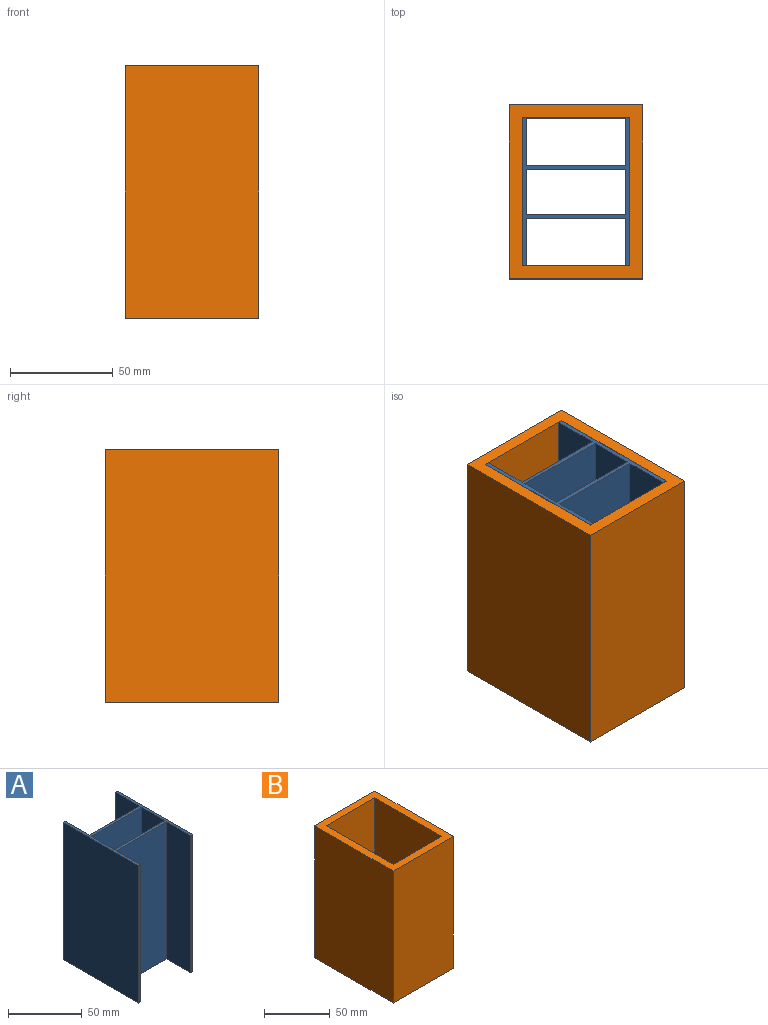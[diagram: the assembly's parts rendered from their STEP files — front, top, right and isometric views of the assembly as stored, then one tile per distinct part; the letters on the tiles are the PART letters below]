
ASSEMBLY  parts=2 mates=1
PART A: 18 faces, bbox 52.2x72x113.6 mm
  f0: plane 113.6x48.2mm, normal (0,1,0), area 5475.5mm2, adj f1,f15,f16,f17
  f1: plane 113.6x22mm, normal (1,0,0), area 2499.2mm2, adj f0,f2,f16,f17
  f2: plane 113.6x48.2mm, normal (0,-1,0), area 5475.5mm2, adj f1,f15,f16,f17
  f3: plane 113.6x72mm, normal (-1,0,0), area 8179.2mm2, adj f4,f14,f16,f17
  f4: plane 113.6x2mm, normal (0,-1,0), area 227.2mm2, adj f3,f5,f16,f17
  f5: plane 113.6x23mm, normal (1,0,0), area 2612.8mm2, adj f4,f6,f16,f17
  f6: plane 113.6x48.2mm, normal (0,-1,0), area 5475.5mm2, adj f5,f7,f16,f17
  f7: plane 113.6x23mm, normal (-1,0,0), area 2612.8mm2, adj f6,f8,f16,f17
  f8: plane 113.6x2mm, normal (0,-1,0), area 227.2mm2, adj f7,f9,f16,f17
  f9: plane 113.6x72mm, normal (1,0,0), area 8179.2mm2, adj f8,f10,f16,f17
  f10: plane 113.6x2mm, normal (0,1,0), area 227.2mm2, adj f9,f11,f16,f17
  f11: plane 113.6x23mm, normal (-1,0,0), area 2612.8mm2, adj f10,f12,f16,f17
  f12: plane 113.6x48.2mm, normal (0,1,0), area 5475.5mm2, adj f11,f13,f16,f17
  f13: plane 113.6x23mm, normal (1,0,0), area 2612.8mm2, adj f12,f14,f16,f17
  f14: plane 113.6x2mm, normal (0,1,0), area 227.2mm2, adj f3,f13,f16,f17
  f15: plane 113.6x22mm, normal (-1,0,0), area 2499.2mm2, adj f0,f2,f16,f17
  f16: plane 72x52.2mm, normal (0,0,1), area 480.8mm2, adj f0,f1,f2,f3,f4,f5,f6,f7
  f17: plane 72x52.2mm, normal (0,0,-1), area 480.8mm2, adj f0,f1,f2,f3,f4,f5,f6,f7
PART B: 10 faces, bbox 64.9x84.6x123 mm
  f0: plane 123x52.46mm, normal (0,1,0), area 6452.6mm2, adj f1,f7,f8,f9
  f1: plane 123x72.18mm, normal (1,0,0), area 8878.1mm2, adj f0,f2,f8,f9
  f2: plane 123x52.46mm, normal (0,-1,0), area 6452.6mm2, adj f1,f7,f8,f9
  f3: plane 123x84.6mm, normal (-1,0,0), area 10405.8mm2, adj f4,f6,f8,f9
  f4: plane 123x64.88mm, normal (0,-1,0), area 7980.2mm2, adj f3,f5,f8,f9
  f5: plane 123x84.6mm, normal (1,0,0), area 10405.8mm2, adj f4,f6,f8,f9
  f6: plane 123x64.88mm, normal (0,1,0), area 7980.2mm2, adj f3,f5,f8,f9
  f7: plane 123x72.18mm, normal (-1,0,0), area 8878.1mm2, adj f0,f2,f8,f9
  f8: plane 84.6x64.88mm, normal (0,0,1), area 1702.3mm2, adj f0,f1,f2,f3,f4,f5,f6,f7
  f9: plane 84.6x64.88mm, normal (0,0,-1), area 1702.3mm2, adj f0,f1,f2,f3,f4,f5,f6,f7
PLACE A rot(axis=(1,0,0),180deg) t=(-15.48,162.58,179.08)mm
PLACE B t=(-15.48,162.58,56.08)mm
MATE fastened A.f17 <-> B.f8  axis (0,0,-1) through (-15.48,162.58,179.08)mm
